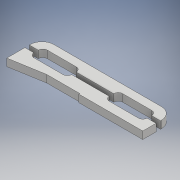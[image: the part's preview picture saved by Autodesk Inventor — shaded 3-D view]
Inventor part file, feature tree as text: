
AUTODESK INVENTOR PART (.ipt)
format: ipt  version: 2019.2 (Build 232265000, 265)  size: 153,088 bytes
history: native  units: mm
features: other x3, plane x1, split x1, move_body x1
ambient origin geometry x8: Origin, YZ Plane, XZ Plane, XY Plane, X Axis, Y Axis, Z Axis, Center Point
bodies: Solid1 (feature_tree), Solid2 (feature_tree), Solid3 (feature_tree)
feature tree (6):
  other  "Swingarm.ipt"
  plane  "Work Plane1"
  split  "Split1"
  move_body  "Move Body1"
  other  "BrakePlate::Swingarm.ipt"
  other  "TaggingFeature1"
